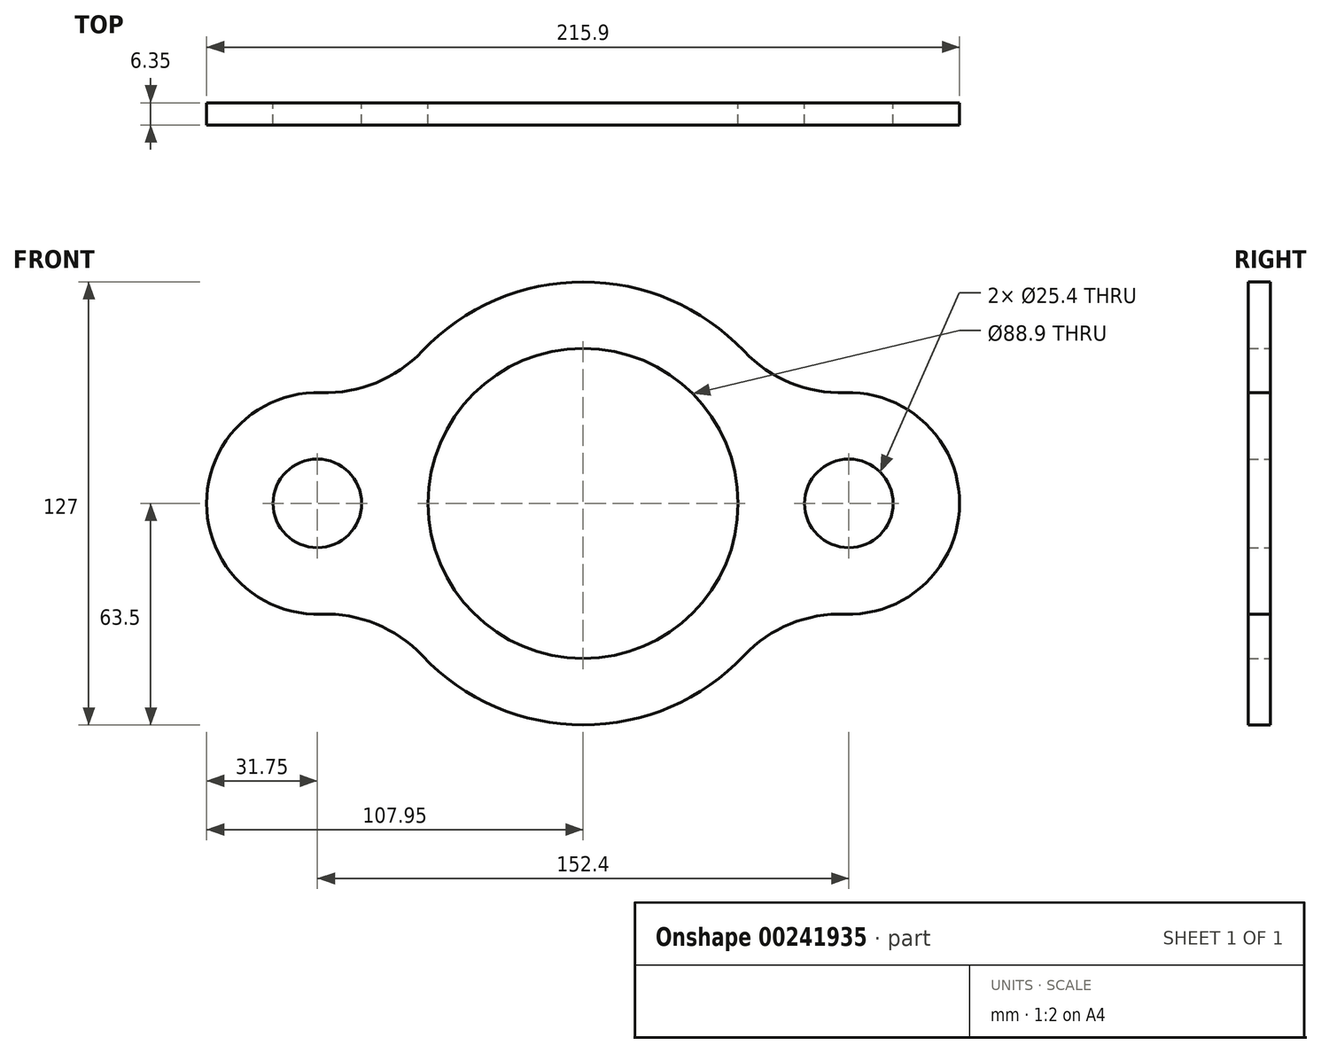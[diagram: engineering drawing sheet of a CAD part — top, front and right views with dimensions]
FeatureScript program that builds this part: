
annotation { "Feature Type Name" : "Feature", "Feature Type Description" : "" }
export const myFeature = defineFeature(function(context is Context, id is Id, definition is map)
    precondition{}
    {
        {
            var Q0;
            Q0=qCreatedBy(makeId("Front.planeOp"),FACE);
            var sketch = newSketch(context, id + "F0", { "sketchPlane" : qUnion([Q0])});
            skCircle(sketch, "E0", {"center": v(0, 0) * mm, "radius": 44.45 * mm});
            skCircle(sketch, "E1", {"center": v(-76.2, 0) * mm, "radius": 12.7 * mm});
            skCircle(sketch, "E2", {"center": v(76.2, 0) * mm, "radius": 12.7 * mm});
            skArc(sketch, "E3", {"start": v(75.12, -31.73) * mm, "mid": v(107.95, 0) * mm, "end": v(75.12, 31.73) * mm});
            skArc(sketch, "E4", {"start": v(-75.12, 31.73) * mm, "mid": v(-107.95, 0) * mm, "end": v(-75.12, -31.73) * mm});
            skArc(sketch, "E5", {"start": v(-46.14, -43.63) * mm, "mid": v(0, -63.5) * mm, "end": v(46.14, -43.63) * mm});
            skArc(sketch, "E6", {"start": v(46.14, 43.63) * mm, "mid": v(0, 63.5) * mm, "end": v(-46.14, 43.63) * mm});
            skPoint(sketch, "E7.visualSharp", {"position": v(-57.94, 25.98) * mm});
            skArc(sketch, "E7.filletArc", {"start": v(-75.12, 31.73) * mm, "mid": v(-59.35, 34.56) * mm, "end": v(-46.14, 43.63) * mm});
            skPoint(sketch, "E8.visualSharp", {"position": v(-57.94, -25.98) * mm});
            skArc(sketch, "E8.filletArc", {"start": v(-46.14, -43.63) * mm, "mid": v(-59.35, -34.56) * mm, "end": v(-75.12, -31.73) * mm});
            skPoint(sketch, "E9.visualSharp", {"position": v(57.94, 25.98) * mm});
            skArc(sketch, "E9.filletArc", {"start": v(46.14, 43.63) * mm, "mid": v(59.35, 34.56) * mm, "end": v(75.12, 31.73) * mm});
            skPoint(sketch, "E10.visualSharp", {"position": v(57.94, -25.98) * mm});
            skArc(sketch, "E10.filletArc", {"start": v(75.12, -31.73) * mm, "mid": v(59.35, -34.56) * mm, "end": v(46.14, -43.63) * mm});
            skSolve(sketch);
        }
        {
            var Q0;
            Q0 = qSketchRegion(id + "F0", true);
            extrude(context, id + "F1", {"entities" : qUnion([Q0]), "depth" : 6.35 * mm});
        }
    });
